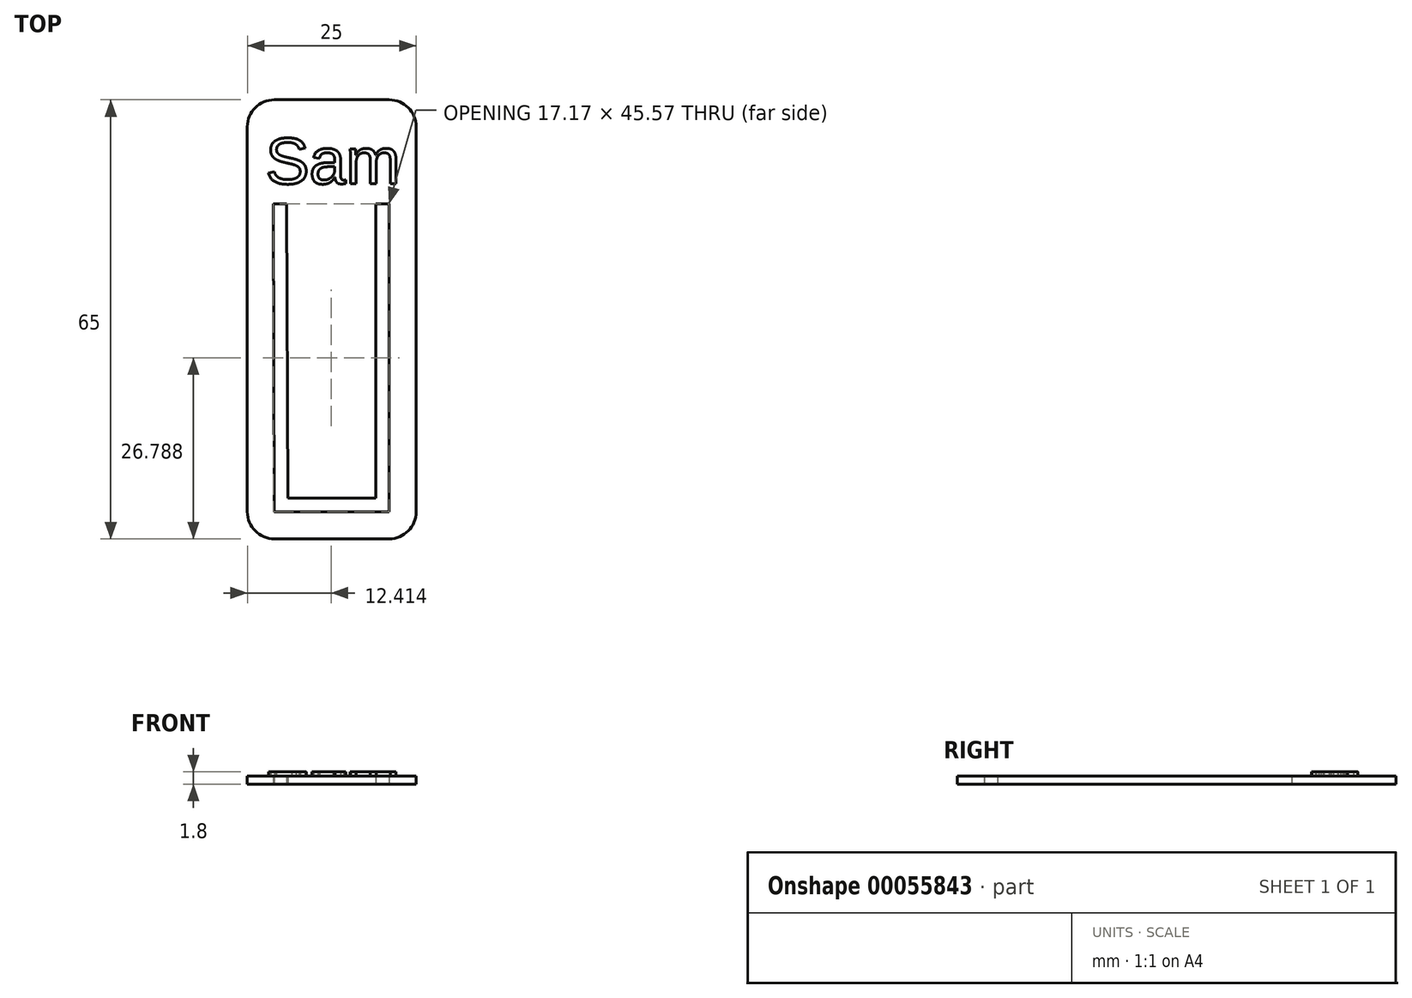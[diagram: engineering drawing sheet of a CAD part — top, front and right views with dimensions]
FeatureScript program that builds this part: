
annotation { "Feature Type Name" : "Feature", "Feature Type Description" : "" }
export const myFeature = defineFeature(function(context is Context, id is Id, definition is map)
    precondition{}
    {
        {
            var Q0;
            Q0=qCreatedBy(makeId("Top.planeOp"),FACE);
            var sketch = newSketch(context, id + "F0", { "sketchPlane" : qUnion([Q0])});
            skLineSegment(sketch, "E0.bottom", {"start": v(-7.08, 28.18) * mm, "end": v(9.92, 28.18) * mm});
            skLineSegment(sketch, "E0.top", {"start": v(-7.08, -36.82) * mm, "end": v(9.92, -36.82) * mm});
            skLineSegment(sketch, "E0.left", {"start": v(-11.08, 24.18) * mm, "end": v(-11.08, -32.82) * mm});
            skLineSegment(sketch, "E0.right", {"start": v(13.92, 24.18) * mm, "end": v(13.92, -32.82) * mm});
            skPoint(sketch, "E1.visualSharp", {"position": v(-11.08, 28.18) * mm});
            skArc(sketch, "E1.filletArc", {"start": v(-7.08, 28.18) * mm, "mid": v(-9.91, 27.01) * mm, "end": v(-11.08, 24.18) * mm});
            skPoint(sketch, "E2.visualSharp", {"position": v(13.92, 28.18) * mm});
            skArc(sketch, "E2.filletArc", {"start": v(13.92, 24.18) * mm, "mid": v(12.74, 27.01) * mm, "end": v(9.92, 28.18) * mm});
            skPoint(sketch, "E3.visualSharp", {"position": v(13.92, -36.82) * mm});
            skArc(sketch, "E3.filletArc", {"start": v(9.92, -36.82) * mm, "mid": v(12.74, -35.65) * mm, "end": v(13.92, -32.82) * mm});
            skPoint(sketch, "E4.visualSharp", {"position": v(-11.08, -36.82) * mm});
            skArc(sketch, "E4.filletArc", {"start": v(-11.08, -32.82) * mm, "mid": v(-9.91, -35.65) * mm, "end": v(-7.08, -36.82) * mm});
            skLineSegment(sketch, "E5", {"start": v(-7.25, 12.75) * mm, "end": v(-7.08, -32.82) * mm});
            skLineSegment(sketch, "E6", {"start": v(9.92, -32.82) * mm, "end": v(9.92, 12.75) * mm});
            skLineSegment(sketch, "E7", {"start": v(-7.08, -32.82) * mm, "end": v(9.92, -32.82) * mm});
            skLineSegment(sketch, "E8.0", {"start": v(7.92, -30.82) * mm, "end": v(7.92, 12.75) * mm});
            skLineSegment(sketch, "E8.1", {"start": v(-5.1, -30.82) * mm, "end": v(7.92, -30.82) * mm});
            skLineSegment(sketch, "E8.2", {"start": v(-5.25, 12.75) * mm, "end": v(-5.1, -30.82) * mm});
            skLineSegment(sketch, "E9", {"start": v(-7.25, 12.75) * mm, "end": v(-5.25, 12.75) * mm});
            skLineSegment(sketch, "E10", {"start": v(7.92, 12.75) * mm, "end": v(9.92, 12.75) * mm});
            skSolve(sketch);
        }
        {
            var Q0;
            Q0=makeQuery(id+"F0.imprint","IMPRINT",FACE,{"disambiguationData":[TD([[makeQuery(id+"F0.imprint","IMPRINT",EDGE,{"derivedFrom":sQuery(id+"F0.wireOp",EDGE,"E0.bottom")}),-1.0]])]});
            extrude(context, id + "F1", {"entities" : qUnion([Q0]), "depth" : 1.2 * mm});
        }
        {
            var Q0;
            Q0=qCreatedBy(makeId("Top.planeOp"),FACE);
            var sketch = newSketch(context, id + "F2", { "sketchPlane" : qUnion([Q0])});
            skText(sketch, "E11", { "text": "Sam", "fontName": "Arimo-Regular.ttf"});
            const initialGuessF2  = {"E11": [-0.0084, 0.01575, 1, 0, 0.007]};
            skSetInitialGuess(sketch, initialGuessF2);
            skSolve(sketch);
        }
        {
            var Q0;
            Q0 = qSketchRegion(id + "F2", true);
            extrude(context, id + "F3", {"entities" : qUnion([Q0]), "operationType" : NewBodyOperationType.ADD, "depth" : 1.8 * mm});
        }
    });
